# Revit family: ONYX servitude gauche
name_source: partatom
category: Modèles génériques
units: mm (PartAtom-declared; Revit-internal decimal feet)

## family parameters
Basée sur le plan de construction = Non
Cote de connecteur circulaire = Utiliser le diamètre
Couper avec des vides une fois chargée = Non
Numéro OmniClass = 23.75.70.17.34
Partagée = Non
Peut héberger une armature = Non
Point de calcul de pièce = Non
Titre OmniClass = Unit Heaters
Toujours verticalement = Oui
Type d'élément = Normal

## types (18) — shared parameters
Fabricant = AIRCALO
Servitude droite = Non
Servitude gauche = Oui
Ø = 34 mm

## per-type parameters (varying)
| type | Base | Console pivotante | Equerre | Equerre arriere | Equerre coté | Equerre inv | Grille | Modèle | Option Froid | Puissance | Tension | Ventilateur | console |
| NY2_A mono | ONYX base 1.1 : NY2A | Console pivotante : NY207 | Equerre : NY212 | 263 mm  [stored 0.862861 ft] | 87 mm  [stored 0.285433 ft] | Equerre inv : NY212 | Grille : 206 | ONYX 2A mono | Option froid : NY208 | 129 VA | 220 V | Ventilateur : diam350 | 86 mm  [stored 0.282152 ft] |
| NY3_A mono | ONYX base 1.1 : NY3A | Console pivotante : NY307 | Equerre : NY212 | 263 mm  [stored 0.862861 ft] | 92 mm  [stored 0.301837 ft] | Equerre inv : NY212 | Grille : 306 | ONYX 3A mono | Option froid : NY308 | 250 VA | 220 V | Ventilateur : diam400 | 87 mm  [stored 0.285433 ft] |
| NY4_A mono | ONYX base 1.1 : NY4A | Console pivotante : NY407 | Equerre : NY212 | 263 mm  [stored 0.862861 ft] | 92 mm  [stored 0.301837 ft] | Equerre inv : NY212 | Grille : 406 | ONYX 4A mono | Option froid : NY408 | 250 VA | 220 V | Ventilateur : diam450 | 96 mm  [stored 0.314961 ft] |
| NY5_A mono | ONYX base 1.1 : NY5A | Console pivotante : NY507 | Equerre : NY612 | 293 mm | 102 mm | Equerre inv : NY612 | Grille : 506 | ONYX 5A mono | Option froid : NY508 | 250 VA | 220 V | Ventilateur : diam550 | 96 mm  [stored 0.314961 ft] |
| NY6_A mono | ONYX base 1.1 : NY6A | Console pivotante : NY607 | Equerre : NY612 | 293 mm | 102 mm | Equerre inv : NY612 | Grille : 606 | ONYX 6A mono | Option froid : NY608 | 400 VA | 220 V | Ventilateur : diam630 | 106 mm  [stored 0.347769 ft] |
| NY2_B mono | ONYX base 1.1 : NY2B | Console pivotante : NY207 | Equerre : NY212 | 263 mm  [stored 0.862861 ft] | 87 mm  [stored 0.285433 ft] | Equerre inv : NY212 | Grille : 206 | ONYX 2B mono | Option froid : NY208 | 205 VA | 220 V | Ventilateur : diam400 | 86 mm  [stored 0.282152 ft] |
| NY3_B mono | ONYX base 1.1 : NY3B | Console pivotante : NY307 | Equerre : NY212 | 263 mm  [stored 0.862861 ft] | 92 mm  [stored 0.301837 ft] | Equerre inv : NY212 | Grille : 306 | ONYX 3B mono | Option froid : NY308 | 250 VA | 220 V | Ventilateur : diam450 | 87 mm  [stored 0.285433 ft] |
| NY4_B mono | ONYX base 1.1 : NY4B | Console pivotante : NY407 | Equerre : NY212 | 263 mm  [stored 0.862861 ft] | 92 mm  [stored 0.301837 ft] | Equerre inv : NY212 | Grille : 406 | ONYX 4B mono | Option froid : NY408 | 250 VA | 220 V | Ventilateur : diam550 | 96 mm  [stored 0.314961 ft] |
| NY5_B mono | ONYX base 1.1 : NY5B | Console pivotante : NY507 | Equerre : NY612 | 293 mm | 102 mm | Equerre inv : NY612 | Grille : 506 | ONYX 5B mono | Option froid : NY508 | 400 VA | 220 V | Ventilateur : diam630 | 96 mm  [stored 0.314961 ft] |
| NY6_B tri | ONYX base 1.1 : NY6B | Console pivotante : NY607 | Equerre : NY612 | 293 mm | 102 mm | Equerre inv : NY612 | Grille : 606 | ONYX 6B tri | Option froid : NY608 | 900 VA | 380 V | Ventilateur : diam710 | 106 mm  [stored 0.347769 ft] |
| NY2_B tri | ONYX base 1.1 : NY2B | Console pivotante : NY207 | Equerre : NY212 | 263 mm  [stored 0.862861 ft] | 87 mm  [stored 0.285433 ft] | Equerre inv : NY212 | Grille : 206 | ONYX 2B tri | Option froid : NY208 | 205 VA | 380 V | Ventilateur : diam400 | 86 mm  [stored 0.282152 ft] |
| NY3_A tri | ONYX base 1.1 : NY3A | Console pivotante : NY307 | Equerre : NY212 | 263 mm  [stored 0.862861 ft] | 92 mm  [stored 0.301837 ft] | Equerre inv : NY212 | Grille : 306 | ONYX 3A tri | Option froid : NY308 | 250 VA | 380 V | Ventilateur : diam400 | 87 mm  [stored 0.285433 ft] |
| NY3_B tri | ONYX base 1.1 : NY3B | Console pivotante : NY307 | Equerre : NY212 | 263 mm  [stored 0.862861 ft] | 92 mm  [stored 0.301837 ft] | Equerre inv : NY212 | Grille : 306 | ONYX 3B tri | Option froid : NY308 | 250 VA | 380 V | Ventilateur : diam450 | 87 mm  [stored 0.285433 ft] |
| NY4_A tri | ONYX base 1.1 : NY4A | Console pivotante : NY407 | Equerre : NY212 | 263 mm  [stored 0.862861 ft] | 92 mm  [stored 0.301837 ft] | Equerre inv : NY212 | Grille : 406 | ONYX 4A tri | Option froid : NY408 | 250 VA | 380 V | Ventilateur : diam450 | 96 mm  [stored 0.314961 ft] |
| NY4_B tri | ONYX base 1.1 : NY4B | Console pivotante : NY407 | Equerre : NY212 | 263 mm  [stored 0.862861 ft] | 92 mm  [stored 0.301837 ft] | Equerre inv : NY212 | Grille : 406 | ONYX 4B tri | Option froid : NY408 | 230 VA | 380 V | Ventilateur : diam550 | 96 mm  [stored 0.314961 ft] |
| NY5_A tri | ONYX base 1.1 : NY5A | Console pivotante : NY507 | Equerre : NY612 | 293 mm | 102 mm | Equerre inv : NY612 | Grille : 506 | ONYX 5A tri | Option froid : NY508 | 230 VA | 380 V | Ventilateur : diam550 | 96 mm  [stored 0.314961 ft] |
| NY5_B tri | ONYX base 1.1 : NY5B | Console pivotante : NY507 | Equerre : NY612 | 293 mm | 102 mm | Equerre inv : NY612 | Grille : 506 | ONYX 5B tri | Option froid : NY508 | 435 VA | 380 V | Ventilateur : diam630 | 96 mm  [stored 0.314961 ft] |
| NY6_A tri | ONYX base 1.1 : NY6A | Console pivotante : NY607 | Equerre : NY612 | 293 mm | 102 mm | Equerre inv : NY612 | Grille : 606 | ONYX 6A tri | Option froid : NY608 | 435 VA | 380 V | Ventilateur : diam630 | 106 mm  [stored 0.347769 ft] |

note: [stored X ft] marks values corroborated as IEEE doubles in the binary element streams (Revit-internal decimal feet)
